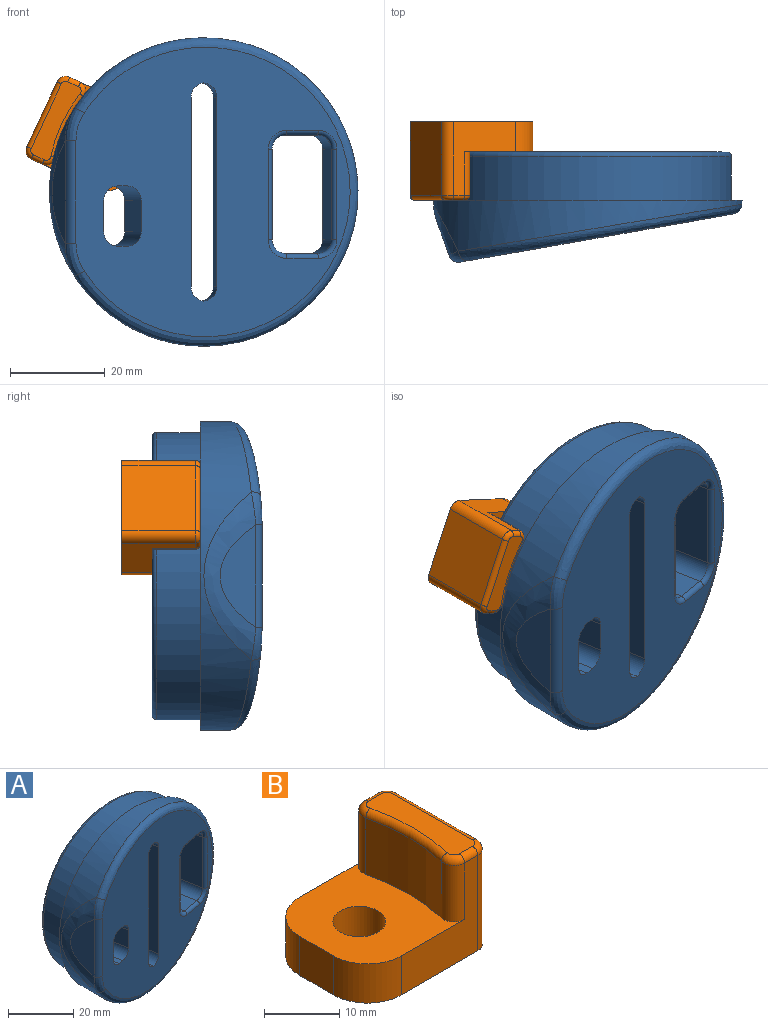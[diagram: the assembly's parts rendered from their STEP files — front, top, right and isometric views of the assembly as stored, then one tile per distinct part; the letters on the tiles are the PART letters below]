
ASSEMBLY  parts=2 mates=1
PART A: 71 faces, bbox 66x25.9x66 mm
  f0: plane 61x57.78mm, normal (0.17,-0.98,0), area 2182.9mm2, adj f6,f7,f17,f18,f19,f20,f25,f26
  f1: plane 59.05x59.05mm, normal (0,1,0), area 750.1mm2, adj f8,f9,f10,f11,f12,f13,f14,f15
  f2: cylinder r=30.29mm len=60.58mm, axis (0,1,0), area 1743.3mm2, adj f4,f65
  f3: cylinder r=32.5mm len=65mm, axis (0,1,0), area 1005.1mm2, adj f4,f26,f67
  f4: plane 65x65mm, normal (0,1,0), area 436mm2, adj f2,f3
  f5: plane 21.53x7.54mm, normal (-0.94,-0.34,0), area 116.6mm2, adj f25,f67
  f6: plane 40x4.13mm, normal (0.98,0.17,0), area 167.6mm2, adj f0,f16,f36,f38
  f7: plane 40x4.13mm, normal (-0.98,-0.17,0), area 167.6mm2, adj f0,f16,f35,f37
  f8: plane 15.37x14.84mm, normal (0,0,-1), area 178.8mm2, adj f1,f9,f15,f16
  f9: cylinder r=6.35mm len=17.57mm, axis (0.17,-0.98,0), area 161.2mm2, adj f1,f8,f10,f16
  f10: plane 40.66x16.49mm, normal (0.98,0.17,0), area 679.6mm2, adj f1,f9,f11,f16,f49,f51,f53
  f11: cylinder r=6.35mm len=17.57mm, axis (0.17,-0.98,0), area 161.2mm2, adj f1,f10,f12,f16
  f12: plane 15.37x14.84mm, normal (0,0,1), area 178.8mm2, adj f1,f11,f13,f16
  f13: cylinder r=6.35mm len=14.33mm, axis (0.17,-0.98,0), area 128.4mm2, adj f1,f12,f14,f16
  f14: plane 40.64x12.12mm, normal (-0.98,-0.17,0), area 500.3mm2, adj f1,f13,f15,f16
  f15: cylinder r=6.35mm len=14.33mm, axis (0.17,-0.98,0), area 128.4mm2, adj f1,f8,f14,f16
  f16: plane 53.34x24.64mm, normal (-0.17,0.98,0), area 1054.1mm2, adj f6,f7,f8,f9,f10,f11,f12,f13
  f17: plane 20.62x5.61mm, normal (0,0,1), area 41.5mm2, adj f0,f27,f30,f48
  f18: plane 19.62x6.7mm, normal (-0.98,-0.17,0), area 133.4mm2, adj f0,f27,f28,f51
  f19: plane 20.62x5.61mm, normal (0,0,-1), area 41.5mm2, adj f0,f28,f29,f56
  f20: plane 21.32x6.7mm, normal (0.98,0.17,0), area 145mm2, adj f0,f29,f30,f52
  f21: plane 12.36x8.78mm, normal (0,0,-1), area 80.1mm2, adj f31,f34,f42,f60
  f22: plane 19x13.22mm, normal (0.98,0.17,0), area 255.1mm2, adj f33,f34,f39,f57
  f23: plane 12.36x8.78mm, normal (0,0,1), area 80.1mm2, adj f32,f33,f43,f61
  f24: plane 19x10.32mm, normal (-0.98,-0.17,0), area 199.2mm2, adj f31,f32,f46,f64
  f25: cylinder r=2mm len=21.53mm, axis (0,0,-1), area 60.1mm2, adj f0,f5,f66,f68
  f26: bspline ~64.91x59.71mm, area 504.3mm2, adj f0,f3,f66,f68
  f27: cylinder r=3mm len=20.8mm, axis (-0.17,0.98,0), area 95.1mm2, adj f0,f17,f18,f47,f49
  f28: cylinder r=3mm len=20.8mm, axis (-0.17,0.98,0), area 95.1mm2, adj f0,f18,f19,f53,f55
  f29: cylinder r=3mm len=21.84mm, axis (0.17,-0.98,0), area 100.3mm2, adj f0,f19,f20,f54
  f30: cylinder r=3mm len=21.84mm, axis (0.17,-0.98,0), area 100.3mm2, adj f0,f17,f20,f50
  f31: cylinder r=3mm len=11.71mm, axis (-0.17,0.98,0), area 51.5mm2, adj f21,f24,f44,f62
  f32: cylinder r=3mm len=11.71mm, axis (0.17,-0.98,0), area 51.5mm2, adj f23,f24,f45,f63
  f33: cylinder r=3mm len=13.75mm, axis (-0.17,0.98,0), area 61.2mm2, adj f22,f23,f41,f59
  f34: cylinder r=3mm len=13.75mm, axis (0.17,-0.98,0), area 61.2mm2, adj f21,f22,f40,f58
  f35: cylinder r=3mm len=4.61mm, axis (-0.17,0.98,0), area 18.7mm2, adj f0,f7,f16,f36
  f36: cylinder r=3mm len=4.61mm, axis (0.17,-0.98,0), area 18.7mm2, adj f0,f6,f16,f35
  f37: cylinder r=3mm len=4.61mm, axis (0.17,-0.98,0), area 18.7mm2, adj f0,f7,f16,f38
  f38: cylinder r=3mm len=4.61mm, axis (-0.17,0.98,0), area 18.7mm2, adj f0,f6,f16,f37
  f39: cylinder r=2mm len=19mm, axis (0,0,-1), area 53.1mm2, adj f1,f22,f40,f41
  f40: bspline ~5.96x5.22mm, area 17.5mm2, adj f1,f34,f39,f42
  f41: bspline ~5.96x5mm, area 17.5mm2, adj f1,f33,f39,f43
  f42: cylinder r=2mm len=6.8mm, axis (-1,0,0), area 21.4mm2, adj f1,f21,f40,f44
  f43: cylinder r=2mm len=6.8mm, axis (1,0,0), area 21.4mm2, adj f1,f23,f41,f45
  f44: bspline ~5.08x5mm, area 19.6mm2, adj f1,f31,f42,f46
  f45: bspline ~5.3x5mm, area 19.6mm2, adj f1,f32,f43,f46
  f46: cylinder r=2mm len=19mm, axis (0,0,1), area 66.3mm2, adj f1,f24,f44,f45
  f47: bspline ~3.8x2.95mm, area 7.1mm2, adj f1,f27,f48,f49
  f48: bspline ~2.03x1mm, area 3.3mm2, adj f1,f17,f47,f50
  f49: bspline ~1.41x1.17mm, area 1.9mm2, adj f10,f27,f47,f51
  f50: bspline ~4.06x4mm, area 8mm2, adj f1,f30,f48,f52
  f51: bspline ~6.7x1.14mm, area 10.2mm2, adj f10,f18,f49,f53
  f52: bspline ~6.7x0.99mm, area 9.5mm2, adj f1,f20,f50,f54
  f53: bspline ~1.41x1.16mm, area 1.9mm2, adj f10,f28,f51,f55
  f54: bspline ~4.06x4mm, area 8mm2, adj f1,f29,f52,f56
  f55: bspline ~3.8x2.95mm, area 7.1mm2, adj f1,f28,f53,f56
  f56: bspline ~2.03x1mm, area 3.3mm2, adj f1,f19,f54,f55
  f57: cylinder r=1mm len=19mm, axis (0,0,1), area 29.8mm2, adj f0,f22,f58,f59
  f58: torus R=4mm, axis (0.17,-0.98,0), area 8.3mm2, adj f0,f34,f57,f60
  f59: torus R=4mm, axis (0.17,-0.98,0), area 8.3mm2, adj f0,f33,f57,f61
  f60: cylinder r=1mm len=6.77mm, axis (0.98,0.17,0), area 10.5mm2, adj f0,f21,f58,f62
  f61: cylinder r=1mm len=6.77mm, axis (-0.98,-0.17,0), area 10.5mm2, adj f0,f23,f59,f63
  f62: torus R=4mm, axis (0.17,-0.98,0), area 8.3mm2, adj f0,f31,f60,f64
  f63: torus R=4mm, axis (0.17,-0.98,0), area 8.3mm2, adj f0,f32,f61,f64
  f64: cylinder r=1mm len=19mm, axis (0,0,-1), area 29.8mm2, adj f0,f24,f62,f63
  f65: torus R=29.29mm, axis (0,-1,0), area 295.4mm2, adj f1,f2
  f66: bspline ~9.48x5.09mm, area 21.6mm2, adj f0,f25,f26,f67
  f67: bspline ~35.4x13.39mm, area 165.5mm2, adj f3,f5,f66,f68
  f68: bspline ~8.63x4.56mm, area 21.6mm2, adj f0,f25,f26,f67
  f69: cylinder r=2.65mm len=12mm, axis (0,1,0), area 199.8mm2, adj f1,f70
  f70: plane 5.3x5.3mm, normal (0,1,0), area 22.1mm2, adj f69
PART B: 23 faces, bbox 22.9x19.4x16.5 mm
  f0: plane 15.51x14.38mm, normal (0,1,0), area 114.1mm2, adj f2,f6,f9,f12,f13,f19
  f1: plane 15.51x14.38mm, normal (0,-1,0), area 114.1mm2, adj f2,f6,f10,f11,f14,f18
  f2: plane 19.05x18.25mm, normal (0,0,1), area 264.2mm2, adj f0,f1,f3,f4,f8,f9,f10,f13
  f3: plane 6.35x6.35mm, normal (-1,0,0), area 40.3mm2, adj f2,f6,f13,f14
  f4: cylinder r=3.5mm len=7mm, axis (0,0,-1), area 139.6mm2, adj f2,f6
  f5: plane 15.51x15.05mm, normal (1,0,0), area 233.4mm2, adj f6,f11,f12,f15
  f6: plane 22.73x19.05mm, normal (0,0,-1), area 375.5mm2, adj f0,f1,f3,f4,f5,f11,f12,f13
  f7: plane 17.05x4.48mm, normal (0,0,1), area 66.7mm2, adj f15,f16,f17,f18,f19,f20,f21,f22
  f8: cylinder r=30.1mm len=14.11mm, axis (0,0,1), area 130.5mm2, adj f2,f9,f10,f22
  f9: cylinder r=2mm len=9.16mm, axis (0,0,1), area 33.1mm2, adj f0,f2,f8,f21
  f10: cylinder r=2mm len=9.16mm, axis (0,0,1), area 33.1mm2, adj f1,f2,f8,f20
  f11: cylinder r=2mm len=15.51mm, axis (0,0,1), area 48.7mm2, adj f1,f5,f6,f16
  f12: cylinder r=2mm len=15.51mm, axis (0,0,-1), area 48.7mm2, adj f0,f5,f6,f17
  f13: cylinder r=6.35mm len=6.35mm, axis (0,0,1), area 63.3mm2, adj f0,f2,f3,f6
  f14: cylinder r=6.35mm len=6.35mm, axis (0,0,-1), area 63.3mm2, adj f1,f2,f3,f6
  f15: cylinder r=1mm len=15.05mm, axis (0,-1,0), area 23.6mm2, adj f5,f7,f16,f17
  f16: torus R=1mm, axis (0,0,1), area 4mm2, adj f7,f11,f15,f18
  f17: torus R=1mm, axis (0,0,1), area 4mm2, adj f7,f12,f15,f19
  f18: cylinder r=1mm len=2.48mm, axis (-1,0,0), area 3.9mm2, adj f1,f7,f16,f20
  f19: cylinder r=1mm len=2.48mm, axis (1,0,0), area 3.9mm2, adj f0,f7,f17,f21
  f20: torus R=1mm, axis (0,0,1), area 4.6mm2, adj f7,f10,f18,f22
  f21: torus R=1mm, axis (0,0,1), area 4.6mm2, adj f7,f9,f19,f22
  f22: torus R=31.1mm, axis (0,0,1), area 22.6mm2, adj f7,f8,f20,f21
PLACE A t=(-67.81,-3.58,29.41)mm
PLACE B rot(axis=(0.15,-0.7,0.7),162.4deg) t=(-90.74,2.77,36.65)mm
MATE revolute B.f4 <-> A.f69  axis (0,-1,0) through (-88.55,-3.58,39.57)mm
